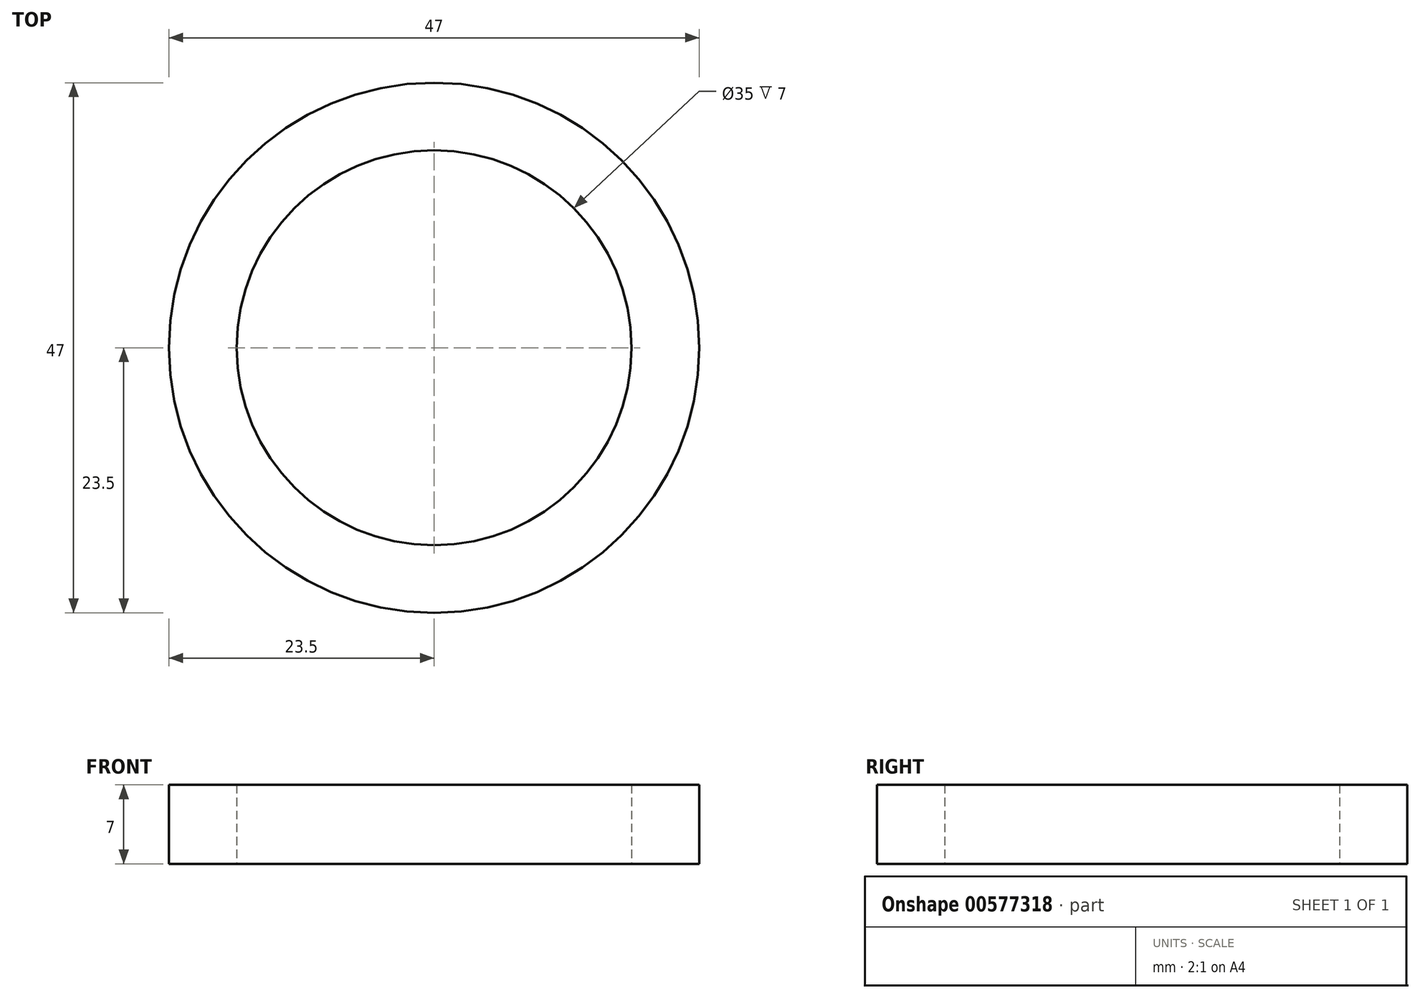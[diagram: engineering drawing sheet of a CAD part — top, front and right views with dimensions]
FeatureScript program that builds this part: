
annotation { "Feature Type Name" : "Feature", "Feature Type Description" : "" }
export const myFeature = defineFeature(function(context is Context, id is Id, definition is map)
    precondition{}
    {
        {
            var Q0;
            Q0=qCreatedBy(makeId("Top.planeOp"),FACE);
            var sketch = newSketch(context, id + "F0", { "sketchPlane" : qUnion([Q0])});
            skCircle(sketch, "E0", {"center": v(0, 0) * mm, "radius": 17.5 * mm});
            skCircle(sketch, "E1", {"center": v(0, 0) * mm, "radius": 23.5 * mm});
            skSolve(sketch);
        }
        {
            var Q0;
            Q0=makeQuery(id+"F0.imprint","IMPRINT",FACE,{"disambiguationData":[TD([[makeQuery(id+"F0.imprint","IMPRINT",EDGE,{"derivedFrom":sQuery(id+"F0.wireOp",EDGE,"E0")}),-1.0]])]});
            extrude(context, id + "F1", {"entities" : qUnion([Q0]), "depth" : 7 * mm, "offsetDistance" : 25.4 * mm});
        }
    });
